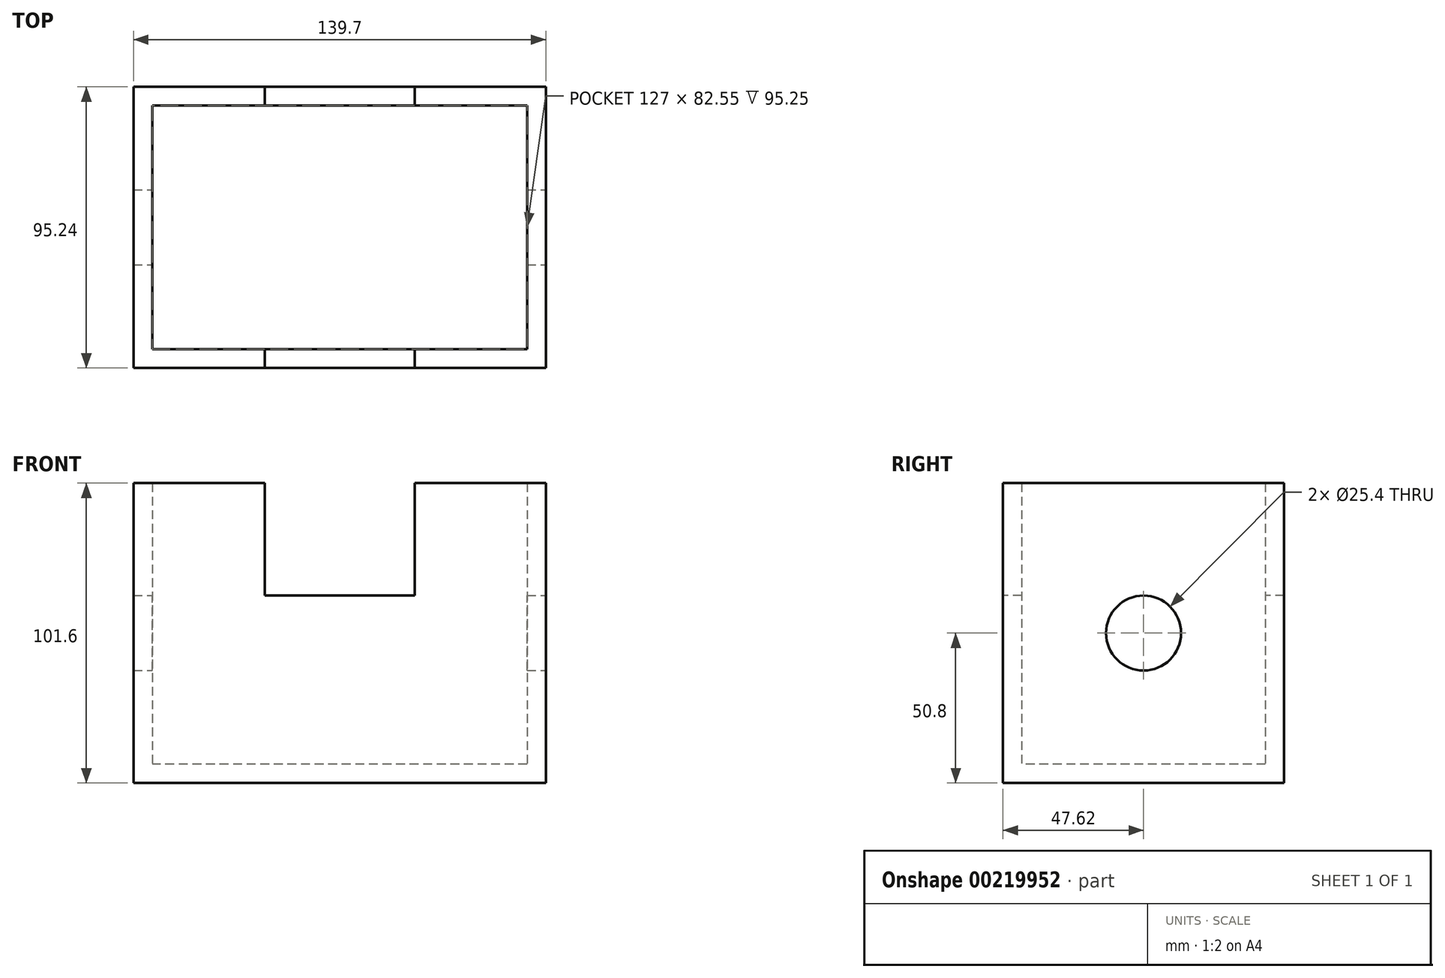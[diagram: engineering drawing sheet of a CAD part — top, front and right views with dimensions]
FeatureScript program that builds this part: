
annotation { "Feature Type Name" : "Feature", "Feature Type Description" : "" }
export const myFeature = defineFeature(function(context is Context, id is Id, definition is map)
    precondition{}
    {
        {
            var Q0;
            Q0=qCreatedBy(makeId("Top.planeOp"),FACE);
            var sketch = newSketch(context, id + "F0", { "sketchPlane" : qUnion([Q0])});
            skLineSegment(sketch, "E0.bottom", {"start": v(69.85, 47.63) * mm, "end": v(-69.85, 47.63) * mm});
            skLineSegment(sketch, "E0.top", {"start": v(69.85, -47.63) * mm, "end": v(-69.85, -47.63) * mm});
            skLineSegment(sketch, "E0.left", {"start": v(69.85, 47.63) * mm, "end": v(69.85, -47.63) * mm});
            skLineSegment(sketch, "E0.right", {"start": v(-69.85, 47.63) * mm, "end": v(-69.85, -47.63) * mm});
            skPoint(sketch, "E0.middle", {"position": v(0, 0) * mm});
            skSolve(sketch);
        }
        {
            var Q0;
            Q0 = qSketchRegion(id + "F0", true);
            extrude(context, id + "F1", {"entities" : qUnion([Q0]), "depth" : 101.6 * mm});
        }
        {
            var Q0;
            Q0=makeQuery(id+"F1.opExtrude","CAP_FACE",FACE,{"disambiguationData":[OSD([sQuery(id+"F0.wireOp",EDGE,"E0.bottom"),sQuery(id+"F0.wireOp",EDGE,"E0.top"),sQuery(id+"F0.wireOp",EDGE,"E0.left"),sQuery(id+"F0.wireOp",EDGE,"E0.right")])],"isStart":false});
            shell(context, id + "F2", {"entities" : qUnion([Q0]), "thickness" : 6.35 * mm});
        }
        {
            var Q0;
            Q0=makeQuery(id+"F1.opExtrude","SWEPT_FACE",FACE,{"disambiguationData":[OSD([sQuery(id+"F0.wireOp",EDGE,"E0.top")])]});
            var sketch = newSketch(context, id + "F3", { "sketchPlane" : qUnion([Q0])});
            skLineSegment(sketch, "E1.bottom", {"start": v(-25.4, 101.6) * mm, "end": v(25.4, 101.6) * mm});
            skLineSegment(sketch, "E1.top", {"start": v(-25.4, 63.5) * mm, "end": v(25.4, 63.5) * mm});
            skLineSegment(sketch, "E1.left", {"start": v(-25.4, 101.6) * mm, "end": v(-25.4, 63.5) * mm});
            skLineSegment(sketch, "E1.right", {"start": v(25.4, 101.6) * mm, "end": v(25.4, 63.5) * mm});
            skSolve(sketch);
        }
        {
            var Q0;
            Q0 = qSketchRegion(id + "F3", true);
            extrude(context, id + "F4", {"entities" : qUnion([Q0]), "operationType" : NewBodyOperationType.REMOVE, "oppositeDirection" : true, "depth" : 101.6 * mm});
        }
        {
            var Q0;
            Q0=makeQuery(id+"F1.opExtrude","SWEPT_FACE",FACE,{"disambiguationData":[OSD([sQuery(id+"F0.wireOp",EDGE,"E0.left")])]});
            var sketch = newSketch(context, id + "F5", { "sketchPlane" : qUnion([Q0])});
            skCircle(sketch, "E2", {"center": v(0, 50.8) * mm, "radius": 12.7 * mm});
            skPoint(sketch, "E2.centerSnap0", {"position": v(0, 101.6) * mm});
            skSolve(sketch);
        }
        {
            var Q0;
            Q0 = qSketchRegion(id + "F5", true);
            extrude(context, id + "F6", {"entities" : qUnion([Q0]), "operationType" : NewBodyOperationType.REMOVE, "oppositeDirection" : true, "depth" : 177.8 * mm});
        }
    });
